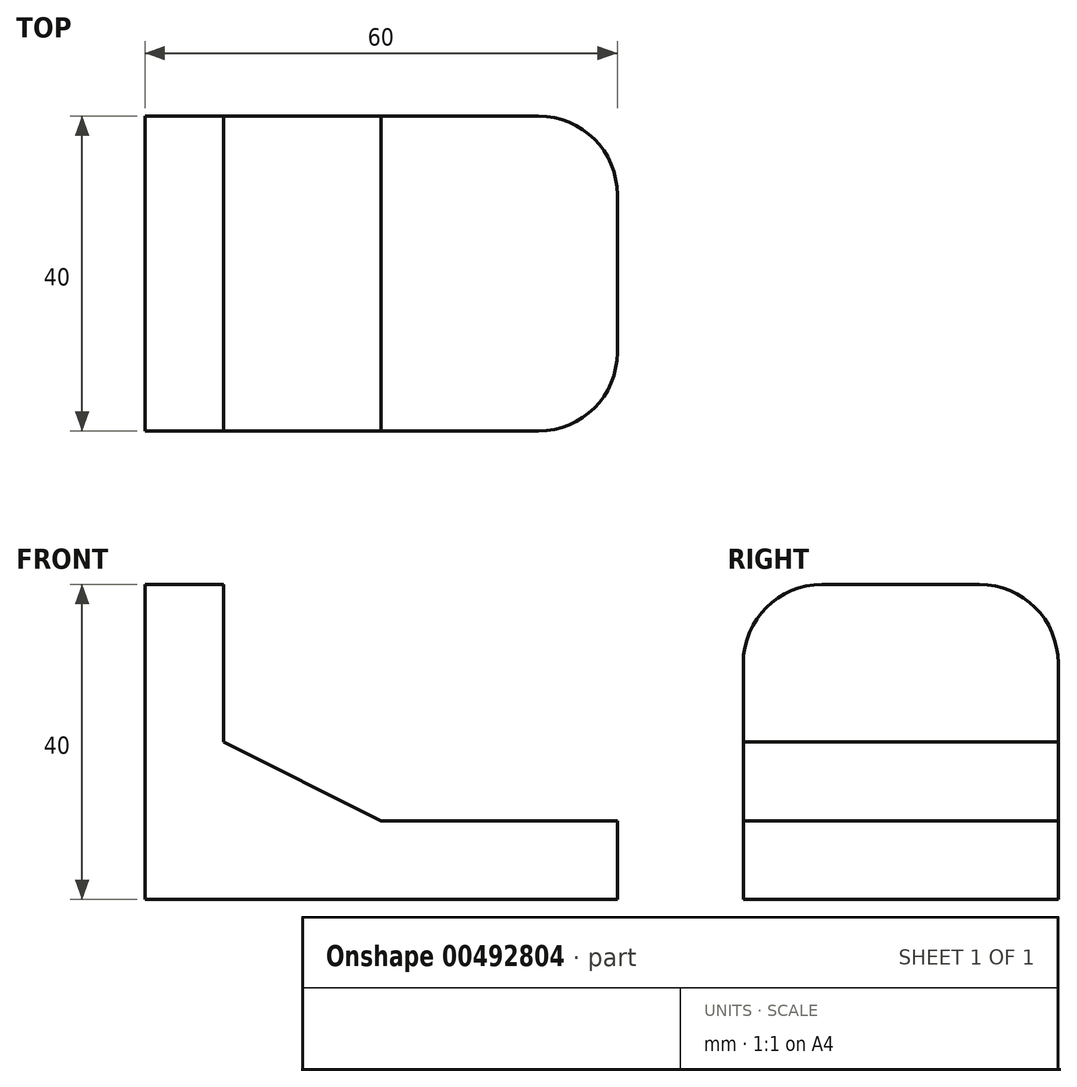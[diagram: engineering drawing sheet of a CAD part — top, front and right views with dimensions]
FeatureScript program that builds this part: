
annotation { "Feature Type Name" : "Feature", "Feature Type Description" : "" }
export const myFeature = defineFeature(function(context is Context, id is Id, definition is map)
    precondition{}
    {
        {
            var Q0;
            Q0=qCreatedBy(makeId("Front.planeOp"),FACE);
            var sketch = newSketch(context, id + "F0", { "sketchPlane" : qUnion([Q0])});
            skLineSegment(sketch, "E0", {"start": v(0, 0) * mm, "end": v(60, 0) * mm});
            skLineSegment(sketch, "E1", {"start": v(60, 0) * mm, "end": v(60, 10) * mm});
            skLineSegment(sketch, "E2", {"start": v(60, 10) * mm, "end": v(30, 10) * mm});
            skLineSegment(sketch, "E3", {"start": v(30, 10) * mm, "end": v(10, 20) * mm});
            skLineSegment(sketch, "E4", {"start": v(10, 20) * mm, "end": v(10, 40) * mm});
            skLineSegment(sketch, "E5", {"start": v(10, 40) * mm, "end": v(0, 40) * mm});
            skLineSegment(sketch, "E6", {"start": v(0, 40) * mm, "end": v(0, 0) * mm});
            skSolve(sketch);
        }
        {
            var Q0;
            Q0 = qSketchRegion(id + "F0", true);
            extrude(context, id + "F1", {"entities" : qUnion([Q0]), "depth" : 40 * mm});
        }
        {
            var Q0;
            Q0=makeQuery(id+"F1.opExtrude","CAP_EDGE",EDGE,{"disambiguationData":[OSD([sQuery(id+"F0.wireOp",EDGE,"E1")])],"isStart":false});
            var Q1;
            Q1=makeQuery(id+"F1.opExtrude","CAP_EDGE",EDGE,{"disambiguationData":[OSD([sQuery(id+"F0.wireOp",EDGE,"E1")])],"isStart":true});
            var Q2;
            Q2=makeQuery(id+"F1.opExtrude","CAP_EDGE",EDGE,{"disambiguationData":[OSD([sQuery(id+"F0.wireOp",EDGE,"E5")])],"isStart":false});
            var Q3;
            Q3=makeQuery(id+"F1.opExtrude","CAP_EDGE",EDGE,{"disambiguationData":[OSD([sQuery(id+"F0.wireOp",EDGE,"E5")])],"isStart":true});
            fillet(context, id + "F2", {"entities" : qUnion([Q0, Q1, Q2, Q3]), "radius" : 10 * mm, "tangentPropagation" : true, "allowEdgeOverflow" : false});
        }
    });
